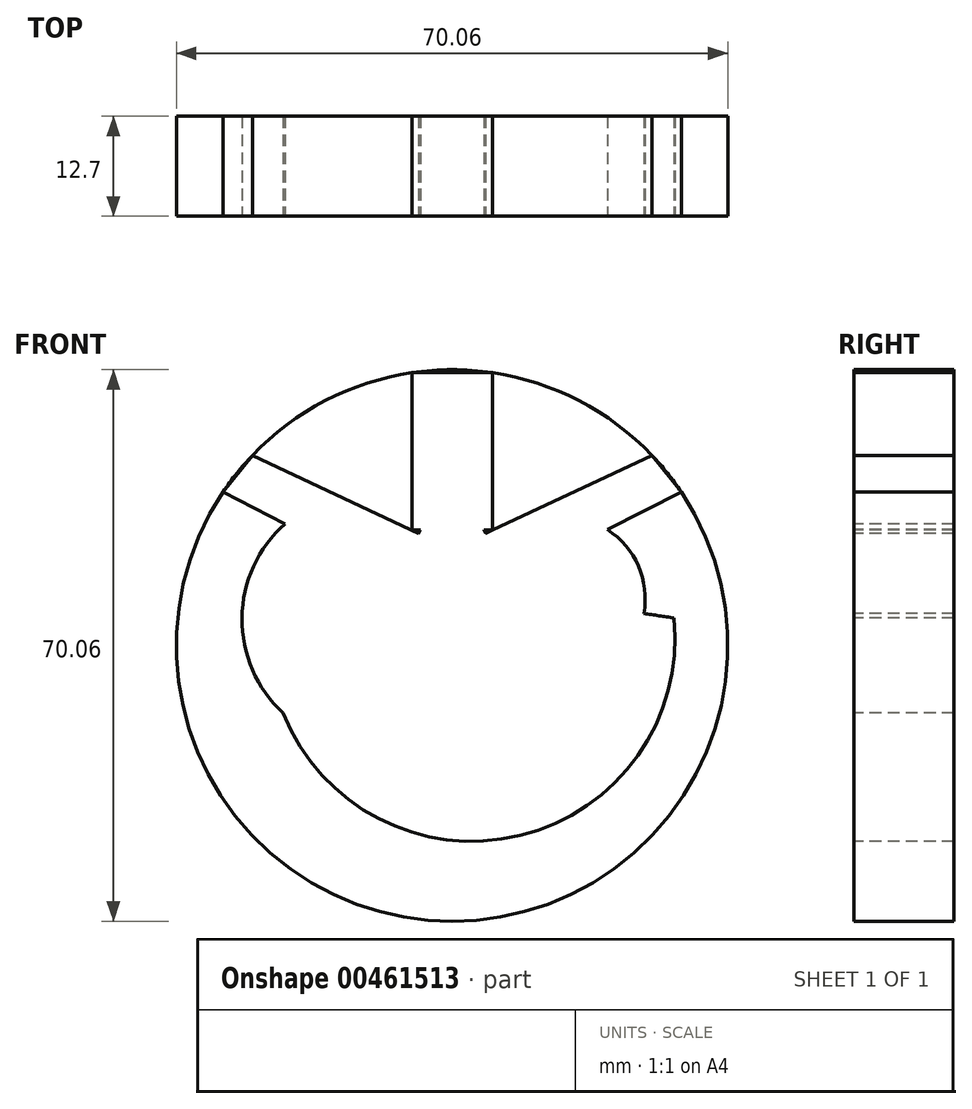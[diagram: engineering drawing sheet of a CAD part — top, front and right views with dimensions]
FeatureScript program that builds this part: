
annotation { "Feature Type Name" : "Feature", "Feature Type Description" : "" }
export const myFeature = defineFeature(function(context is Context, id is Id, definition is map)
    precondition{}
    {
        {
            var Q0;
            Q0=qCreatedBy(makeId("Front.planeOp"),FACE);
            var sketch = newSketch(context, id + "F0", { "sketchPlane" : qUnion([Q0])});
            skCircle(sketch, "E0", {"center": v(0, 0) * mm, "radius": 35.03 * mm});
            skSolve(sketch);
        }
        {
            var Q0;
            Q0 = qSketchRegion(id + "F0", true);
            extrude(context, id + "F1", {"entities" : qUnion([Q0]), "depth" : 12.7 * mm});
        }
        {
            var Q0;
            Q0=makeQuery(id+"F1.opExtrude","CAP_FACE",FACE,{"disambiguationData":[OSD([sQuery(id+"F0.wireOp",EDGE,"E0")])],"isStart":false});
            var sketch = newSketch(context, id + "F2", { "sketchPlane" : qUnion([Q0])});
            skPoint(sketch, "E1", {"position": v(-29.1, 19.5) * mm});
            skPoint(sketch, "E2", {"position": v(-25.37, 24.15) * mm});
            skLineSegment(sketch, "E3", {"start": v(0, -54.57) * mm, "end": v(0, 55.18) * mm, "construction": true});
            skPoint(sketch, "E4.MirrorP", {"position": v(25.37, 24.15) * mm});
            skPoint(sketch, "E5.MirrorP", {"position": v(29.1, 19.5) * mm});
            skPoint(sketch, "E6", {"position": v(0, 12.26) * mm});
            skPoint(sketch, "E7", {"position": v(0, 4.6) * mm});
            skLineSegment(sketch, "E8", {"start": v(-25.37, 24.15) * mm, "end": v(0, 12.26) * mm});
            skLineSegment(sketch, "E9", {"start": v(25.37, 24.15) * mm, "end": v(0, 12.26) * mm});
            skLineSegment(sketch, "E10", {"start": v(29.1, 19.5) * mm, "end": v(0, 4.6) * mm});
            skLineSegment(sketch, "E11", {"start": v(0, 4.6) * mm, "end": v(-29.1, 19.5) * mm});
            skLineSegment(sketch, "E12", {"start": v(-29.1, 19.5) * mm, "end": v(-25.37, 24.15) * mm});
            skLineSegment(sketch, "E13", {"start": v(29.1, 19.5) * mm, "end": v(25.37, 24.15) * mm});
            skSolve(sketch);
        }
        {
            var Q0;
            Q0 = qSketchRegion(id + "F2", true);
            extrude(context, id + "F3", {"entities" : qUnion([Q0]), "operationType" : NewBodyOperationType.REMOVE, "oppositeDirection" : true, "depth" : 25.4 * mm});
        }
        {
            var Q0;
            {var subQ0=sQuery(id+"F0.wireOp",EDGE,"E0");Q0=makeQuery(id+"F3.boolean.opBoolean","SPLIT",FACE,{"disambiguationData":[TD([makeQuery(id+"F3.opExtrude","SWEPT_FACE",FACE,{"disambiguationData":[OSD([sQuery(id+"F2.wireOp",EDGE,"E10")])]})])],"derivedFrom":makeQuery(id+"F1.opExtrude","CAP_FACE",FACE,{"disambiguationData":[OSD([subQ0])],"isStart":false})});}
            var sketch = newSketch(context, id + "F4", { "sketchPlane" : qUnion([Q0])});
            skCircle(sketch, "E14", {"center": v(0, -6.44) * mm, "radius": 16.6 * mm});
            skSolve(sketch);
        }
        {
            var Q0;
            Q0 = qSketchRegion(id + "F4", true);
            extrude(context, id + "F5", {"entities" : qUnion([Q0]), "operationType" : NewBodyOperationType.REMOVE, "oppositeDirection" : true, "depth" : 25.4 * mm});
        }
        {
            var Q0;
            {var subQ0=sQuery(id+"F0.wireOp",EDGE,"E0");Q0=makeQuery(id+"F3.boolean.opBoolean","SPLIT",FACE,{"disambiguationData":[TD([makeQuery(id+"F3.opExtrude","SWEPT_FACE",FACE,{"disambiguationData":[OSD([sQuery(id+"F2.wireOp",EDGE,"E10")])]})])],"derivedFrom":makeQuery(id+"F1.opExtrude","CAP_FACE",FACE,{"disambiguationData":[OSD([subQ0])],"isStart":false})});}
            var sketch = newSketch(context, id + "F6", { "sketchPlane" : qUnion([Q0])});
            skArc(sketch, "E15", {"start": v(-21.22, 15.46) * mm, "mid": v(-26.7, 3.5) * mm, "end": v(-21.46, -8.58) * mm});
            skArc(sketch, "E16", {"start": v(-21.46, -8.58) * mm, "mid": v(8.62, -24.14) * mm, "end": v(28.2, 3.5) * mm});
            skPoint(sketch, "E16.endSnap0", {"position": v(-26.7, 3.5) * mm});
            skArc(sketch, "E17", {"start": v(-21.22, 15.46) * mm, "mid": v(3.2, 8.3) * mm, "end": v(28.2, 3.5) * mm});
            skSolve(sketch);
        }
        {
            var Q0;
            Q0 = qSketchRegion(id + "F6", true);
            extrude(context, id + "F7", {"entities" : qUnion([Q0]), "operationType" : NewBodyOperationType.REMOVE, "oppositeDirection" : true, "depth" : 25.4 * mm});
        }
        {
            var Q0;
            {var subQ0=sQuery(id+"F0.wireOp",EDGE,"E0");Q0=makeQuery(id+"F3.boolean.opBoolean","SPLIT",FACE,{"disambiguationData":[TD([makeQuery(id+"F3.opExtrude","SWEPT_FACE",FACE,{"disambiguationData":[OSD([sQuery(id+"F2.wireOp",EDGE,"E10")])]})])],"derivedFrom":makeQuery(id+"F1.opExtrude","CAP_FACE",FACE,{"disambiguationData":[OSD([subQ0])],"isStart":false})});}
            var sketch = newSketch(context, id + "F8", { "sketchPlane" : qUnion([Q0])});
            skCircle(sketch, "E18", {"center": v(14.04, 5.91) * mm, "radius": 10.48 * mm});
            skSolve(sketch);
        }
        {
            var Q0;
            Q0 = qSketchRegion(id + "F8", true);
            extrude(context, id + "F9", {"entities" : qUnion([Q0]), "operationType" : NewBodyOperationType.REMOVE, "oppositeDirection" : true, "depth" : 25.4 * mm});
        }
        {
            var Q0;
            {var subQ0=sQuery(id+"F0.wireOp",EDGE,"E0");Q0=makeQuery(id+"F3.boolean.opBoolean","SPLIT",FACE,{"disambiguationData":[TD([makeQuery(id+"F3.opExtrude","SWEPT_FACE",FACE,{"disambiguationData":[OSD([sQuery(id+"F2.wireOp",EDGE,"E8")])]})])],"derivedFrom":makeQuery(id+"F1.opExtrude","CAP_FACE",FACE,{"disambiguationData":[OSD([subQ0])],"isStart":false})});}
            var sketch = newSketch(context, id + "F10", { "sketchPlane" : qUnion([Q0])});
            skLineSegment(sketch, "E19.bottom", {"start": v(-5.1, 34.66) * mm, "end": v(5.1, 34.66) * mm});
            skLineSegment(sketch, "E19.top", {"start": v(-5.1, 14.65) * mm, "end": v(5.1, 14.65) * mm});
            skLineSegment(sketch, "E19.left", {"start": v(-5.1, 34.66) * mm, "end": v(-5.1, 14.65) * mm});
            skLineSegment(sketch, "E19.right", {"start": v(5.1, 34.66) * mm, "end": v(5.1, 14.65) * mm});
            skSolve(sketch);
        }
        {
            var Q0;
            Q0 = qSketchRegion(id + "F10", true);
            extrude(context, id + "F11", {"entities" : qUnion([Q0]), "operationType" : NewBodyOperationType.REMOVE, "oppositeDirection" : true, "depth" : 25.4 * mm});
        }
        {
            var Q0;
            {var subQ0=makeQuery(id+"F3.opExtrude","SWEPT_FACE",FACE,{"disambiguationData":[OSD([sQuery(id+"F2.wireOp",EDGE,"E8")])]});var subQ2=sQuery(id+"F0.wireOp",EDGE,"E0");Q0=makeQuery(id+"F11.boolean.opBoolean","SPLIT",FACE,{"disambiguationData":[TD([makeQuery(id+"F3.boolean.opBoolean","COPY",FACE,{"derivedFrom":subQ0})])],"derivedFrom":makeQuery(id+"F3.boolean.opBoolean","SPLIT",FACE,{"disambiguationData":[TD([subQ0])],"derivedFrom":makeQuery(id+"F1.opExtrude","CAP_FACE",FACE,{"disambiguationData":[OSD([subQ2])],"isStart":false})})});}
            var sketch = newSketch(context, id + "F12", { "sketchPlane" : qUnion([Q0])});
            skCircle(sketch, "E20", {"center": v(0, 12.26) * mm, "radius": 4.69 * mm});
            skSolve(sketch);
        }
        {
            var Q0;
            Q0 = qSketchRegion(id + "F12", true);
            extrude(context, id + "F13", {"entities" : qUnion([Q0]), "operationType" : NewBodyOperationType.REMOVE, "oppositeDirection" : true, "depth" : 25.4 * mm});
        }
    });
